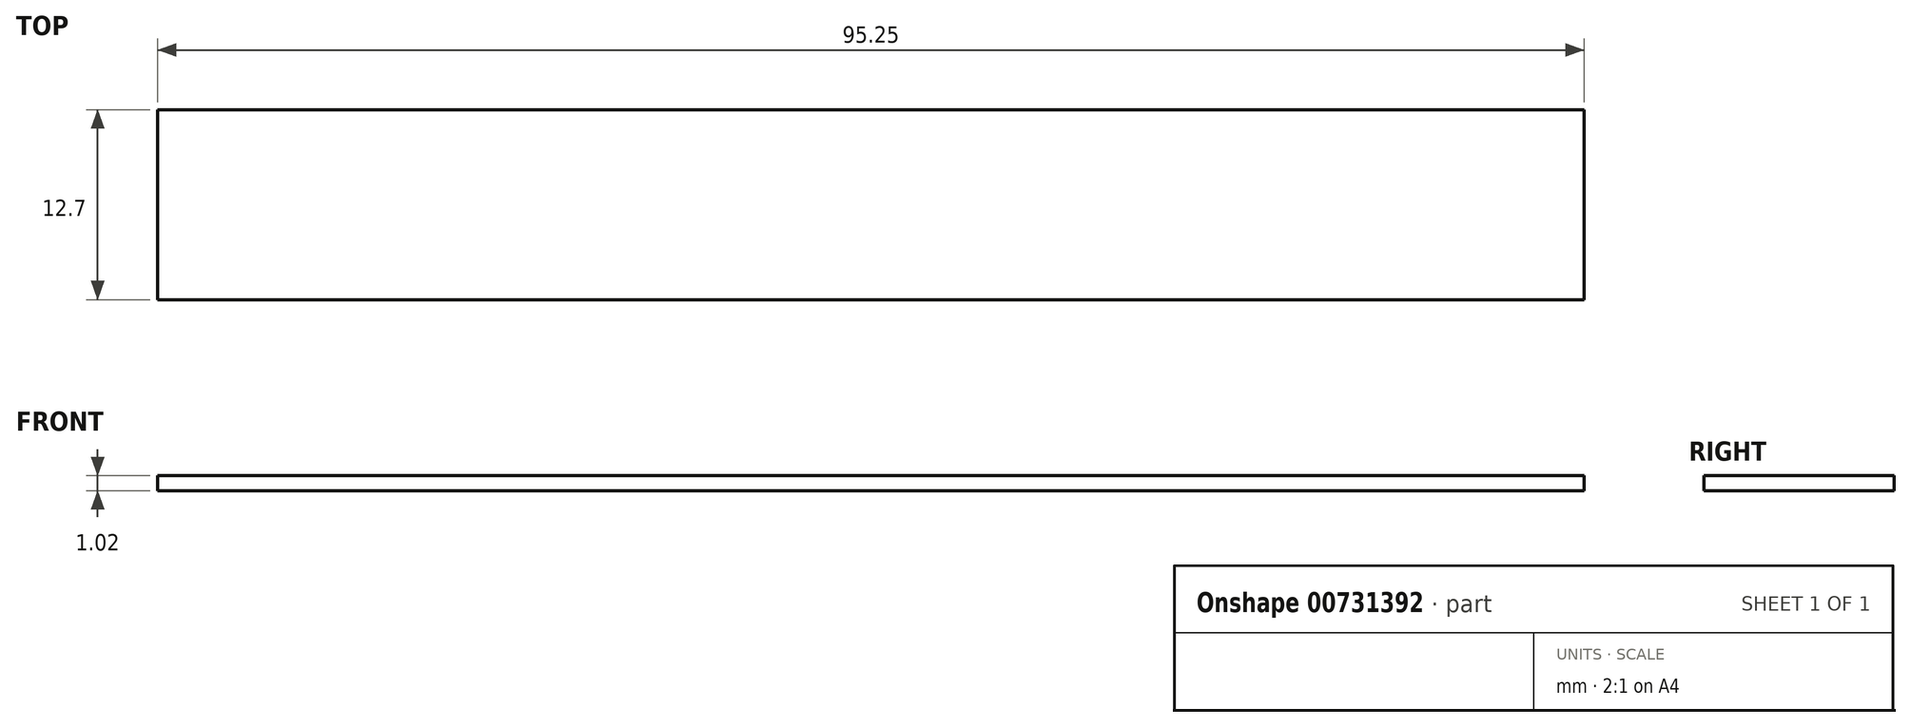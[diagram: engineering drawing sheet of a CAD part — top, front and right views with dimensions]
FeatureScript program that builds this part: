
annotation { "Feature Type Name" : "Feature", "Feature Type Description" : "" }
export const myFeature = defineFeature(function(context is Context, id is Id, definition is map)
    precondition{}
    {
        {
            var Q0;
            Q0=qCreatedBy(makeId("Top.planeOp"),FACE);
            var sketch = newSketch(context, id + "F0", { "sketchPlane" : qUnion([Q0])});
            skLineSegment(sketch, "E0.bottom", {"start": v(0, 0) * mm, "end": v(95.25, 0) * mm});
            skLineSegment(sketch, "E0.top", {"start": v(0, 12.7) * mm, "end": v(95.25, 12.7) * mm});
            skLineSegment(sketch, "E0.left", {"start": v(0, 0) * mm, "end": v(0, 12.7) * mm});
            skLineSegment(sketch, "E0.right", {"start": v(95.25, 0) * mm, "end": v(95.25, 12.7) * mm});
            skSolve(sketch);
        }
        {
            var Q0;
            Q0 = qSketchRegion(id + "F0", true);
            extrude(context, id + "F1", {"entities" : qUnion([Q0]), "depth" : 1.02 * mm, "offsetDistance" : 25.4 * mm});
        }
    });
